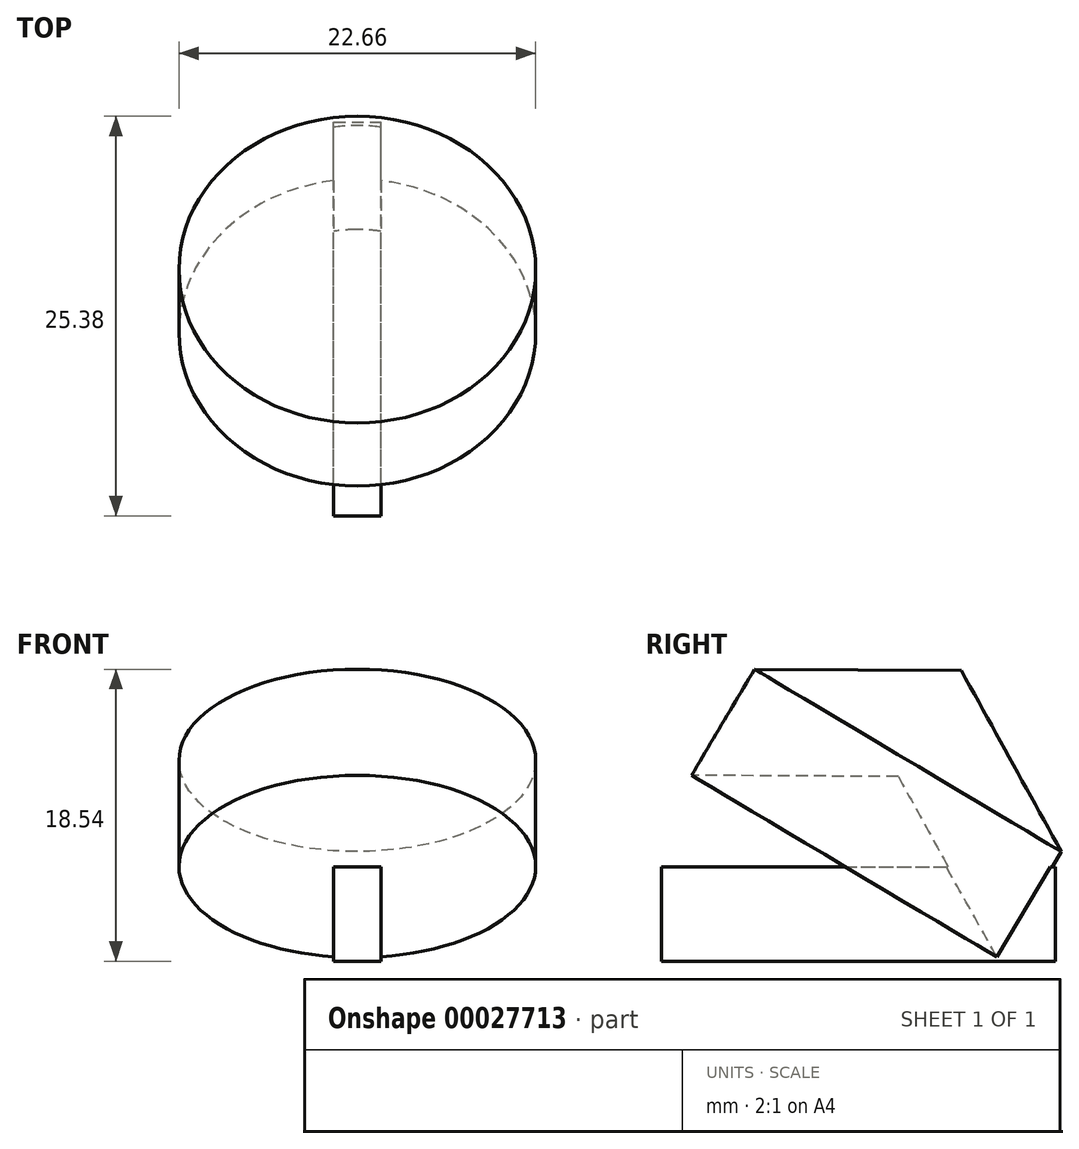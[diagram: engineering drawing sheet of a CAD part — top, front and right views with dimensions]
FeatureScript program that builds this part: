
annotation { "Feature Type Name" : "Feature", "Feature Type Description" : "" }
export const myFeature = defineFeature(function(context is Context, id is Id, definition is map)
    precondition{}
    {
        {
            var Q0;
            Q0=qCreatedBy(makeId("Front.planeOp"),FACE);
            var sketch = newSketch(context, id + "F0", { "sketchPlane" : qUnion([Q0])});
            skLineSegment(sketch, "E0.left", {"start": v(0, 0) * mm, "end": v(0, 0) * mm});
            skLineSegment(sketch, "E1.bottom", {"start": v(-1.5, 3) * mm, "end": v(1.5, 3) * mm});
            skLineSegment(sketch, "E1.top", {"start": v(-1.5, -3) * mm, "end": v(1.5, -3) * mm});
            skLineSegment(sketch, "E1.left", {"start": v(-1.5, 3) * mm, "end": v(-1.5, -3) * mm});
            skLineSegment(sketch, "E1.right", {"start": v(1.5, 3) * mm, "end": v(1.5, -3) * mm});
            skLineSegment(sketch, "E2", {"start": v(-1.5, 0) * mm, "end": v(1.5, 0) * mm, "construction": true});
            skLineSegment(sketch, "E3", {"start": v(0, 3) * mm, "end": v(0, -3) * mm, "construction": true});
            skSolve(sketch);
        }
        {
            var Q0;
            Q0=makeQuery(id+"F0.imprint","IMPRINT",FACE,{"disambiguationData":[TD([[makeQuery(id+"F0.imprint","IMPRINT",EDGE,{"derivedFrom":sQuery(id+"F0.wireOp",EDGE,"E1.bottom")}),-1.0]])]});
            extrude(context, id + "F1", {"entities" : qUnion([Q0]), "depth" : 25 * mm});
        }
        {
            var Q0;
            Q0=qCreatedBy(makeId("Right.planeOp"),FACE);
            var sketch = newSketch(context, id + "F2", { "sketchPlane" : qUnion([Q0])});
            skLineSegment(sketch, "E4", {"start": v(-23.1, 8.8) * mm, "end": v(-19.1, 15.54) * mm});
            skLineSegment(sketch, "E5", {"start": v(-19.1, 15.54) * mm, "end": v(-5.97, 15.47) * mm});
            skLineSegment(sketch, "E6", {"start": v(-5.97, 15.47) * mm, "end": v(-9.97, 8.73) * mm});
            skLineSegment(sketch, "E7", {"start": v(-9.97, 8.73) * mm, "end": v(-23.1, 8.8) * mm});
            skSolve(sketch);
        }
        {
            var Q0;
            Q0=makeQuery(id+"F2.imprint","IMPRINT",FACE,{"disambiguationData":[TD([[makeQuery(id+"F2.imprint","IMPRINT",EDGE,{"derivedFrom":sQuery(id+"F2.wireOp",EDGE,"E4")}),-1.0]])]});
            var Q1;
            Q1=sQuery(id+"F2.wireOp",EDGE,"E6");
            revolve(context, id + "F3", {"operationType" : NewBodyOperationType.ADD, "entities" : qUnion([Q0]), "axis" : qUnion([Q1]), "revolveType" : RevolveType.FULL});
        }
    });
